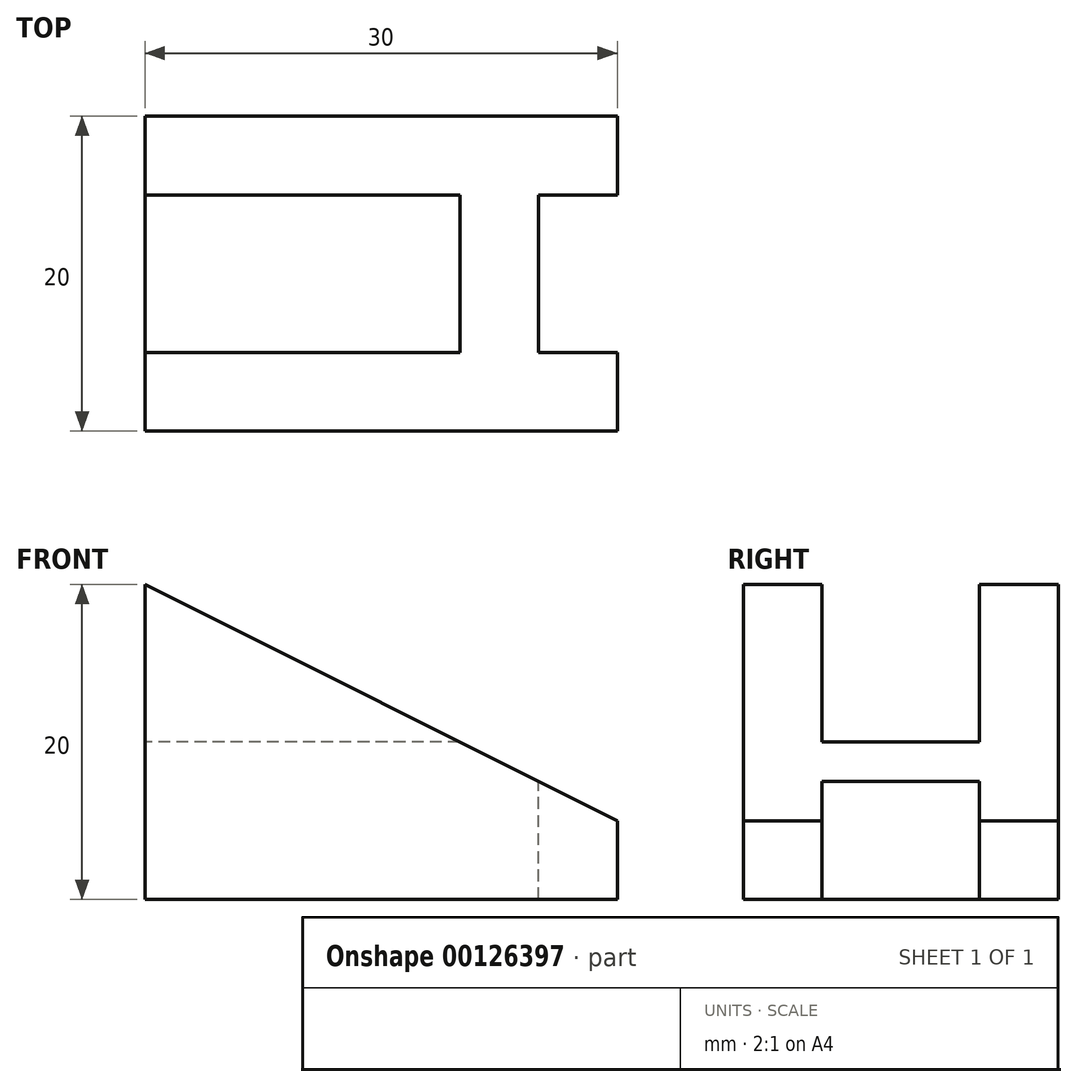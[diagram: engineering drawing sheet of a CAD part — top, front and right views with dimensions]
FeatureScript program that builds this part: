
annotation { "Feature Type Name" : "Feature", "Feature Type Description" : "" }
export const myFeature = defineFeature(function(context is Context, id is Id, definition is map)
    precondition{}
    {
        {
            var Q0;
            Q0=qCreatedBy(makeId("Right.planeOp"),FACE);
            var sketch = newSketch(context, id + "F0", { "sketchPlane" : qUnion([Q0])});
            skLineSegment(sketch, "E0.bottom", {"start": v(0, 0) * mm, "end": v(20, 0) * mm});
            skLineSegment(sketch, "E0.top", {"start": v(0, 20) * mm, "end": v(20, 20) * mm});
            skLineSegment(sketch, "E0.left", {"start": v(0, 0) * mm, "end": v(0, 20) * mm});
            skLineSegment(sketch, "E0.right", {"start": v(20, 0) * mm, "end": v(20, 20) * mm});
            skLineSegment(sketch, "E1.bottom", {"start": v(5, 0) * mm, "end": v(15, 0) * mm});
            skLineSegment(sketch, "E1.top", {"start": v(5, 7.5) * mm, "end": v(15, 7.5) * mm});
            skLineSegment(sketch, "E1.left", {"start": v(5, 0) * mm, "end": v(5, 7.5) * mm});
            skLineSegment(sketch, "E1.right", {"start": v(15, 0) * mm, "end": v(15, 7.5) * mm});
            skSolve(sketch);
        }
        {
            var Q0;
            Q0 = qSketchRegion(id + "F0", true);
            extrude(context, id + "F1", {"entities" : qUnion([Q0]), "depth" : 30 * mm});
        }
        {
            var Q0;
            Q0=makeQuery(id+"F1.opExtrude","CAP_FACE",FACE,{"disambiguationData":[OSD([sQuery(id+"F0.wireOp",EDGE,"E0.bottom"),sQuery(id+"F0.wireOp",EDGE,"E0.top"),sQuery(id+"F0.wireOp",EDGE,"E0.left"),sQuery(id+"F0.wireOp",EDGE,"E0.right"),sQuery(id+"F0.wireOp",EDGE,"E1.bottom")])],"isStart":false});
            var sketch = newSketch(context, id + "F2", { "sketchPlane" : qUnion([Q0])});
            skLineSegment(sketch, "E2.0", {"start": v(5, 0) * mm, "end": v(5, 7.5) * mm});
            skLineSegment(sketch, "E3.0.0", {"start": v(0, 20) * mm, "end": v(0, 0) * mm});
            skLineSegment(sketch, "E3.0.1", {"start": v(5, 0) * mm, "end": v(15, 0) * mm});
            skLineSegment(sketch, "E3.0.2", {"start": v(20, 0) * mm, "end": v(20, 20) * mm});
            skLineSegment(sketch, "E3.0.3", {"start": v(20, 20) * mm, "end": v(0, 20) * mm});
            skLineSegment(sketch, "E4.0", {"start": v(5, 7.5) * mm, "end": v(15, 7.5) * mm});
            skLineSegment(sketch, "E5.0", {"start": v(15, 0) * mm, "end": v(15, 7.5) * mm});
            skSolve(sketch);
        }
        {
            var Q0;
            Q0=makeQuery(id+"F2.imprint","IMPRINT",FACE,{"disambiguationData":[TD([[makeQuery(id+"F2.imprint","IMPRINT",EDGE,{"derivedFrom":sQuery(id+"F2.wireOp",EDGE,"E2.0")}),-1.0]])]});
            extrude(context, id + "F3", {"entities" : qUnion([Q0]), "operationType" : NewBodyOperationType.REMOVE, "oppositeDirection" : true, "depth" : 5 * mm});
        }
        {
            var Q0;
            Q0=makeQuery(id+"F1.opExtrude","SWEPT_FACE",FACE,{"disambiguationData":[OSD([sQuery(id+"F0.wireOp",EDGE,"E0.left")])]});
            var sketch = newSketch(context, id + "F4", { "sketchPlane" : qUnion([Q0])});
            skLineSegment(sketch, "E6.0", {"start": v(30, 0) * mm, "end": v(0, 0) * mm});
            skLineSegment(sketch, "E7", {"start": v(0, 0) * mm, "end": v(0, 5) * mm});
            skLineSegment(sketch, "E8", {"start": v(0, 5) * mm, "end": v(30, 5) * mm});
            skLineSegment(sketch, "E9", {"start": v(30, 5) * mm, "end": v(30, 0) * mm});
            skLineSegment(sketch, "E10", {"start": v(0, 20) * mm, "end": v(30, 5) * mm});
            skSolve(sketch);
        }
        {
            var Q0;
            {var subQ0=sQuery(id+"F4.wireOp",EDGE,"E10");Q0=makeQuery(id+"F4.imprint","IMPRINT",FACE,{"disambiguationData":[TD([[makeQuery(id+"F4.imprint","IMPRINT",EDGE,{"derivedFrom":subQ0}),1.0]])]});}
            extrude(context, id + "F5", {"entities" : qUnion([Q0]), "operationType" : NewBodyOperationType.REMOVE, "endBound" : BoundingType.THROUGH_ALL, "oppositeDirection" : true, "depth" : 25 * mm});
        }
        {
            var Q0;
            Q0=makeQuery(id+"F0.imprint","IMPRINT",FACE,{"disambiguationData":[TD([[makeQuery(id+"F0.imprint","IMPRINT",EDGE,{"derivedFrom":sQuery(id+"F0.wireOp",EDGE,"E0.top")}),-1.0]])]});
            var sketch = newSketch(context, id + "F6", { "sketchPlane" : qUnion([Q0])});
            skLineSegment(sketch, "E11.0", {"start": v(0, 20) * mm, "end": v(5, 20) * mm});
            skLineSegment(sketch, "E12.0", {"start": v(20, 0) * mm, "end": v(20, 20) * mm});
            skLineSegment(sketch, "E13.0", {"start": v(0, 0) * mm, "end": v(0, 20) * mm});
            skLineSegment(sketch, "E14.top", {"start": v(15, 10) * mm, "end": v(5, 10) * mm});
            skLineSegment(sketch, "E14.left", {"start": v(15, 20) * mm, "end": v(15, 10) * mm});
            skLineSegment(sketch, "E14.right", {"start": v(5, 20) * mm, "end": v(5, 10) * mm});
            skLineSegment(sketch, "E15.trimOffspring", {"start": v(15, 20) * mm, "end": v(20, 20) * mm});
            skLineSegment(sketch, "E16", {"start": v(15, 20) * mm, "end": v(5, 20) * mm});
            skLineSegment(sketch, "E17", {"start": v(20, 0) * mm, "end": v(0, 0) * mm});
            skSolve(sketch);
        }
        {
            var Q0;
            Q0=makeQuery(id+"F6.imprint","IMPRINT",FACE,{"disambiguationData":[TD([[makeQuery(id+"F6.imprint","IMPRINT",EDGE,{"derivedFrom":sQuery(id+"F6.wireOp",EDGE,"E14.top")}),-1.0]])]});
            extrude(context, id + "F7", {"entities" : qUnion([Q0]), "operationType" : NewBodyOperationType.REMOVE, "endBound" : BoundingType.THROUGH_ALL, "depth" : 25 * mm});
        }
    });
